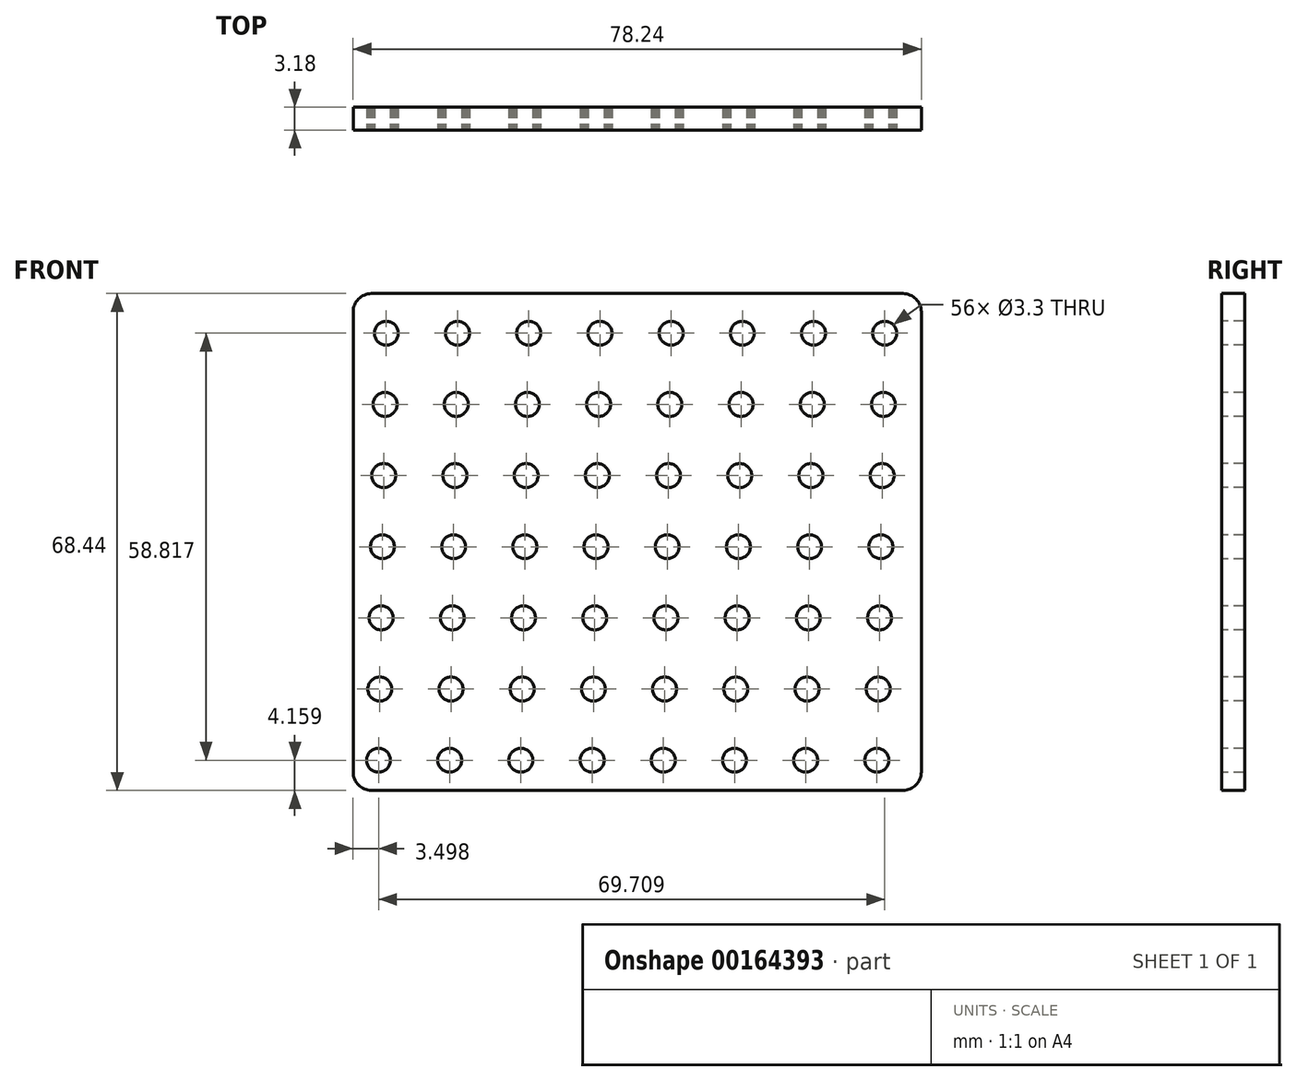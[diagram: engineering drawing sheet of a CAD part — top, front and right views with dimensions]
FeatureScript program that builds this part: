
annotation { "Feature Type Name" : "Feature", "Feature Type Description" : "" }
export const myFeature = defineFeature(function(context is Context, id is Id, definition is map)
    precondition{}
    {
        {
            var Q0;
            Q0=qCreatedBy(makeId("Front.planeOp"),FACE);
            var sketch = newSketch(context, id + "F0", { "sketchPlane" : qUnion([Q0])});
            skLineSegment(sketch, "E0.bottom", {"start": v(39.12, 34.22) * mm, "end": v(-39.12, 34.22) * mm});
            skLineSegment(sketch, "E0.top", {"start": v(39.12, -34.22) * mm, "end": v(-39.12, -34.22) * mm});
            skLineSegment(sketch, "E0.left", {"start": v(39.12, 34.22) * mm, "end": v(39.12, -34.22) * mm});
            skLineSegment(sketch, "E0.right", {"start": v(-39.12, 34.22) * mm, "end": v(-39.12, -34.22) * mm});
            skPoint(sketch, "E0.middle", {"position": v(0, 0) * mm});
            skSolve(sketch);
        }
        {
            var Q0;
            Q0=makeQuery(id+"F0.imprint","IMPRINT",FACE,{"disambiguationData":[TD([[makeQuery(id+"F0.imprint","IMPRINT",EDGE,{"derivedFrom":sQuery(id+"F0.wireOp",EDGE,"E0.bottom")}),1.0]])]});
            extrude(context, id + "F1", {"entities" : qUnion([Q0]), "depth" : 3.17 * mm});
        }
        {
            var Q0;
            Q0=makeQuery(id+"F1.opExtrude","CAP_FACE",FACE,{"disambiguationData":[OSD([sQuery(id+"F0.wireOp",EDGE,"E0.bottom"),sQuery(id+"F0.wireOp",EDGE,"E0.top"),sQuery(id+"F0.wireOp",EDGE,"E0.left"),sQuery(id+"F0.wireOp",EDGE,"E0.right")])],"isStart":false});
            var sketch = newSketch(context, id + "F2", { "sketchPlane" : qUnion([Q0])});
            skCircle(sketch, "E1", {"center": v(-34.54, 28.76) * mm, "radius": 1.65 * mm});
            skCircle(sketch, "E2.1.0.0", {"center": v(-24.74, 28.76) * mm, "radius": 1.65 * mm});
            skCircle(sketch, "E2.2.0.0", {"center": v(-14.94, 28.76) * mm, "radius": 1.65 * mm});
            skCircle(sketch, "E2.3.0.0", {"center": v(-5.13, 28.76) * mm, "radius": 1.65 * mm});
            skCircle(sketch, "E2.4.0.0", {"center": v(4.67, 28.76) * mm, "radius": 1.65 * mm});
            skCircle(sketch, "E2.5.0.0", {"center": v(14.48, 28.76) * mm, "radius": 1.65 * mm});
            skCircle(sketch, "E2.6.0.0", {"center": v(24.28, 28.76) * mm, "radius": 1.65 * mm});
            skCircle(sketch, "E2.7.0.0", {"center": v(34.09, 28.76) * mm, "radius": 1.65 * mm});
            skLineSegment(sketch, "E2.direction1", {"start": v(-34.54, 28.76) * mm, "end": v(-24.74, 28.76) * mm, "construction": true});
            skCircle(sketch, "E3.1.0.0", {"center": v(-34.72, 18.95) * mm, "radius": 1.65 * mm});
            skCircle(sketch, "E3.2.0.0", {"center": v(-34.9, 9.15) * mm, "radius": 1.65 * mm});
            skCircle(sketch, "E3.3.0.0", {"center": v(-35.08, -0.65) * mm, "radius": 1.65 * mm});
            skCircle(sketch, "E3.4.0.0", {"center": v(-35.26, -10.45) * mm, "radius": 1.65 * mm});
            skCircle(sketch, "E3.5.0.0", {"center": v(-35.44, -20.26) * mm, "radius": 1.65 * mm});
            skCircle(sketch, "E3.6.0.0", {"center": v(-35.62, -30.06) * mm, "radius": 1.65 * mm});
            skLineSegment(sketch, "E3.direction1", {"start": v(-34.54, 28.76) * mm, "end": v(-34.72, 18.95) * mm, "construction": true});
            skCircle(sketch, "E4.1.0.0", {"center": v(-24.92, 18.95) * mm, "radius": 1.65 * mm});
            skCircle(sketch, "E4.1.0.1", {"center": v(-25.1, 9.15) * mm, "radius": 1.65 * mm});
            skCircle(sketch, "E4.1.0.2", {"center": v(-25.28, -0.65) * mm, "radius": 1.65 * mm});
            skCircle(sketch, "E4.1.0.3", {"center": v(-25.46, -10.45) * mm, "radius": 1.65 * mm});
            skCircle(sketch, "E4.1.0.4", {"center": v(-25.64, -20.26) * mm, "radius": 1.65 * mm});
            skCircle(sketch, "E4.1.0.5", {"center": v(-25.82, -30.06) * mm, "radius": 1.65 * mm});
            skCircle(sketch, "E4.2.0.0", {"center": v(-15.11, 18.95) * mm, "radius": 1.65 * mm});
            skCircle(sketch, "E4.2.0.1", {"center": v(-15.3, 9.15) * mm, "radius": 1.65 * mm});
            skCircle(sketch, "E4.2.0.2", {"center": v(-15.47, -0.65) * mm, "radius": 1.65 * mm});
            skCircle(sketch, "E4.2.0.3", {"center": v(-15.65, -10.45) * mm, "radius": 1.65 * mm});
            skCircle(sketch, "E4.2.0.4", {"center": v(-15.83, -20.26) * mm, "radius": 1.65 * mm});
            skCircle(sketch, "E4.2.0.5", {"center": v(-16.01, -30.06) * mm, "radius": 1.65 * mm});
            skCircle(sketch, "E4.3.0.0", {"center": v(-5.31, 18.95) * mm, "radius": 1.65 * mm});
            skCircle(sketch, "E4.3.0.1", {"center": v(-5.5, 9.15) * mm, "radius": 1.65 * mm});
            skCircle(sketch, "E4.3.0.2", {"center": v(-5.67, -0.65) * mm, "radius": 1.65 * mm});
            skCircle(sketch, "E4.3.0.3", {"center": v(-5.85, -10.45) * mm, "radius": 1.65 * mm});
            skCircle(sketch, "E4.3.0.4", {"center": v(-6.03, -20.26) * mm, "radius": 1.65 * mm});
            skCircle(sketch, "E4.3.0.5", {"center": v(-6.2, -30.06) * mm, "radius": 1.65 * mm});
            skCircle(sketch, "E4.4.0.0", {"center": v(4.5, 18.95) * mm, "radius": 1.65 * mm});
            skCircle(sketch, "E4.4.0.1", {"center": v(4.31, 9.15) * mm, "radius": 1.65 * mm});
            skCircle(sketch, "E4.4.0.2", {"center": v(4.13, -0.65) * mm, "radius": 1.65 * mm});
            skCircle(sketch, "E4.4.0.3", {"center": v(3.95, -10.45) * mm, "radius": 1.65 * mm});
            skCircle(sketch, "E4.4.0.4", {"center": v(3.78, -20.26) * mm, "radius": 1.65 * mm});
            skCircle(sketch, "E4.4.0.5", {"center": v(3.6, -30.06) * mm, "radius": 1.65 * mm});
            skCircle(sketch, "E4.5.0.0", {"center": v(14.3, 18.95) * mm, "radius": 1.65 * mm});
            skCircle(sketch, "E4.5.0.1", {"center": v(14.12, 9.15) * mm, "radius": 1.65 * mm});
            skCircle(sketch, "E4.5.0.2", {"center": v(13.94, -0.65) * mm, "radius": 1.65 * mm});
            skCircle(sketch, "E4.5.0.3", {"center": v(13.76, -10.45) * mm, "radius": 1.65 * mm});
            skCircle(sketch, "E4.5.0.4", {"center": v(13.58, -20.26) * mm, "radius": 1.65 * mm});
            skCircle(sketch, "E4.5.0.5", {"center": v(13.4, -30.06) * mm, "radius": 1.65 * mm});
            skCircle(sketch, "E4.6.0.0", {"center": v(24.1, 18.95) * mm, "radius": 1.65 * mm});
            skCircle(sketch, "E4.6.0.1", {"center": v(23.92, 9.15) * mm, "radius": 1.65 * mm});
            skCircle(sketch, "E4.6.0.2", {"center": v(23.74, -0.65) * mm, "radius": 1.65 * mm});
            skCircle(sketch, "E4.6.0.3", {"center": v(23.56, -10.45) * mm, "radius": 1.65 * mm});
            skCircle(sketch, "E4.6.0.4", {"center": v(23.38, -20.26) * mm, "radius": 1.65 * mm});
            skCircle(sketch, "E4.6.0.5", {"center": v(23.2, -30.06) * mm, "radius": 1.65 * mm});
            skCircle(sketch, "E4.7.0.0", {"center": v(33.9, 18.95) * mm, "radius": 1.65 * mm});
            skCircle(sketch, "E4.7.0.1", {"center": v(33.73, 9.15) * mm, "radius": 1.65 * mm});
            skCircle(sketch, "E4.7.0.2", {"center": v(33.55, -0.65) * mm, "radius": 1.65 * mm});
            skCircle(sketch, "E4.7.0.3", {"center": v(33.37, -10.45) * mm, "radius": 1.65 * mm});
            skCircle(sketch, "E4.7.0.4", {"center": v(33.19, -20.26) * mm, "radius": 1.65 * mm});
            skCircle(sketch, "E4.7.0.5", {"center": v(33, -30.06) * mm, "radius": 1.65 * mm});
            skLineSegment(sketch, "E4.direction1", {"start": v(-34.72, 18.95) * mm, "end": v(-24.92, 18.95) * mm, "construction": true});
            skSolve(sketch);
        }
        {
            var Q0;
            Q0=sQuery(id+"F2.wireOp",VERTEX,"E4.4.0.4.center");
            var Q1;
            Q1=sQuery(id+"F2.wireOp",VERTEX,"E4.7.0.5.center");
            var Q2;
            Q2=sQuery(id+"F2.wireOp",VERTEX,"E4.1.0.0.center");
            var Q3;
            Q3=sQuery(id+"F2.wireOp",VERTEX,"E4.3.0.4.center");
            var Q4;
            Q4=sQuery(id+"F2.wireOp",VERTEX,"E4.7.0.2.center");
            var Q5;
            Q5=sQuery(id+"F2.wireOp",VERTEX,"E4.1.0.5.center");
            var Q6;
            Q6=sQuery(id+"F2.wireOp",VERTEX,"E4.2.0.3.center");
            var Q7;
            Q7=sQuery(id+"F2.wireOp",VERTEX,"E4.6.0.2.center");
            var Q8;
            Q8=sQuery(id+"F2.wireOp",VERTEX,"E4.3.0.3.center");
            var Q9;
            Q9=sQuery(id+"F2.wireOp",VERTEX,"E4.3.0.2.center");
            var Q10;
            Q10=sQuery(id+"F2.wireOp",VERTEX,"E2.5.0.0.center");
            var Q11;
            Q11=sQuery(id+"F2.wireOp",VERTEX,"E4.4.0.2.center");
            var Q12;
            Q12=sQuery(id+"F2.wireOp",VERTEX,"E3.6.0.0.center");
            var Q13;
            Q13=sQuery(id+"F2.wireOp",VERTEX,"E4.4.0.3.center");
            var Q14;
            Q14=sQuery(id+"F2.wireOp",VERTEX,"E4.7.0.1.center");
            var Q15;
            Q15=sQuery(id+"F2.wireOp",VERTEX,"E4.6.0.0.center");
            var Q16;
            Q16=sQuery(id+"F2.wireOp",VERTEX,"E3.2.0.0.center");
            var Q17;
            Q17=sQuery(id+"F2.wireOp",VERTEX,"E3.5.0.0.center");
            var Q18;
            Q18=sQuery(id+"F2.wireOp",VERTEX,"E4.1.0.4.center");
            var Q19;
            Q19=sQuery(id+"F2.wireOp",VERTEX,"E2.7.0.0.center");
            var Q20;
            Q20=sQuery(id+"F2.wireOp",VERTEX,"E2.6.0.0.center");
            var Q21;
            Q21=sQuery(id+"F2.wireOp",VERTEX,"E2.4.0.0.center");
            var Q22;
            Q22=sQuery(id+"F2.wireOp",VERTEX,"E2.3.0.0.center");
            var Q23;
            Q23=sQuery(id+"F2.wireOp",VERTEX,"E4.7.0.0.center");
            var Q24;
            Q24=sQuery(id+"F2.wireOp",VERTEX,"E4.3.0.1.center");
            var Q25;
            Q25=sQuery(id+"F2.wireOp",VERTEX,"E4.5.0.5.center");
            var Q26;
            Q26=sQuery(id+"F2.wireOp",VERTEX,"E2.2.0.0.center");
            var Q27;
            Q27=sQuery(id+"F2.wireOp",VERTEX,"E2.1.0.0.center");
            var Q28;
            Q28=sQuery(id+"F2.wireOp",VERTEX,"E3.4.0.0.center");
            var Q29;
            Q29=sQuery(id+"F2.wireOp",VERTEX,"E4.1.0.3.center");
            var Q30;
            Q30=sQuery(id+"F2.wireOp",VERTEX,"E4.4.0.1.center");
            var Q31;
            Q31=sQuery(id+"F2.wireOp",VERTEX,"E4.3.0.0.center");
            var Q32;
            Q32=sQuery(id+"F2.wireOp",VERTEX,"E4.6.0.5.center");
            var Q33;
            Q33=sQuery(id+"F2.wireOp",VERTEX,"E4.5.0.4.center");
            var Q34;
            Q34=sQuery(id+"F2.wireOp",VERTEX,"E3.3.0.0.center");
            var Q35;
            Q35=sQuery(id+"F2.wireOp",VERTEX,"E4.4.0.0.center");
            var Q36;
            Q36=sQuery(id+"F2.wireOp",VERTEX,"E4.2.0.5.center");
            var Q37;
            Q37=sQuery(id+"F2.wireOp",VERTEX,"E4.5.0.3.center");
            var Q38;
            Q38=sQuery(id+"F2.wireOp",VERTEX,"E4.6.0.4.center");
            var Q39;
            Q39=sQuery(id+"F2.wireOp",VERTEX,"E4.1.0.2.center");
            var Q40;
            Q40=sQuery(id+"F2.wireOp",VERTEX,"E4.2.0.2.center");
            var Q41;
            Q41=sQuery(id+"F2.wireOp",VERTEX,"E4.5.0.0.center");
            var Q42;
            Q42=sQuery(id+"F2.wireOp",VERTEX,"E4.7.0.4.center");
            var Q43;
            Q43=sQuery(id+"F2.wireOp",VERTEX,"E4.3.0.5.center");
            var Q44;
            Q44=sQuery(id+"F2.wireOp",VERTEX,"E4.2.0.4.center");
            var Q45;
            Q45=sQuery(id+"F2.wireOp",VERTEX,"E1.center");
            var Q46;
            Q46=sQuery(id+"F2.wireOp",VERTEX,"E4.5.0.2.center");
            var Q47;
            Q47=sQuery(id+"F2.wireOp",VERTEX,"E4.6.0.3.center");
            var Q48;
            Q48=sQuery(id+"F2.wireOp",VERTEX,"E4.1.0.1.center");
            var Q49;
            Q49=sQuery(id+"F2.wireOp",VERTEX,"E4.2.0.1.center");
            var Q50;
            Q50=sQuery(id+"F2.wireOp",VERTEX,"E4.4.0.5.center");
            var Q51;
            Q51=sQuery(id+"F2.wireOp",VERTEX,"E4.7.0.3.center");
            var Q52;
            Q52=sQuery(id+"F2.wireOp",VERTEX,"E4.direction1.start");
            var Q53;
            Q53=sQuery(id+"F2.wireOp",VERTEX,"E4.6.0.1.center");
            var Q54;
            Q54=sQuery(id+"F2.wireOp",VERTEX,"E4.2.0.0.center");
            var Q55;
            Q55=sQuery(id+"F2.wireOp",VERTEX,"E4.5.0.1.center");
            var Q56;
            Q56=makeQuery(id+"F1.opExtrude","SWEPT_BODY",BODY,{"disambiguationData":[OSD([sQuery(id+"F0.wireOp",EDGE,"E0.bottom"),sQuery(id+"F0.wireOp",EDGE,"E0.top"),sQuery(id+"F0.wireOp",EDGE,"E0.left"),sQuery(id+"F0.wireOp",EDGE,"E0.right")])]});
            hole(context, id + "F3", {"style" : HoleStyle.SIMPLE, "endStyle" : HoleEndStyle.THROUGH, "holeDiameter" : 3.3 * mm, "locations" : qUnion([Q0, Q1, Q2, Q3, Q4, Q5, Q6, Q7, Q8, Q9, Q10, Q11, Q12, Q13, Q14, Q15, Q16, Q17, Q18, Q19, Q20, Q21, Q22, Q23, Q24, Q25, Q26, Q27, Q28, Q29, Q30, Q31, Q32, Q33, Q34, Q35, Q36, Q37, Q38, Q39, Q40, Q41, Q42, Q43, Q44, Q45, Q46, Q47, Q48, Q49, Q50, Q51, Q52, Q53, Q54, Q55]), "scope" : qUnion([Q56]), "isTappedThrough" : true});
        }
        {
            var Q0;
            Q0=makeQuery(id+"F1.opExtrude","SWEPT_EDGE",EDGE,{"disambiguationData":[OSD([sQuery(id+"F0.wireOp",EDGE,"E0.bottom"),sQuery(id+"F0.wireOp",EDGE,"E0.right")])]});
            var Q1;
            Q1=makeQuery(id+"F1.opExtrude","SWEPT_EDGE",EDGE,{"disambiguationData":[OSD([sQuery(id+"F0.wireOp",EDGE,"E0.top"),sQuery(id+"F0.wireOp",EDGE,"E0.right")])]});
            var Q2;
            Q2=makeQuery(id+"F1.opExtrude","SWEPT_EDGE",EDGE,{"disambiguationData":[OSD([sQuery(id+"F0.wireOp",EDGE,"E0.top"),sQuery(id+"F0.wireOp",EDGE,"E0.left")])]});
            var Q3;
            Q3=makeQuery(id+"F1.opExtrude","SWEPT_EDGE",EDGE,{"disambiguationData":[OSD([sQuery(id+"F0.wireOp",EDGE,"E0.bottom"),sQuery(id+"F0.wireOp",EDGE,"E0.left")])]});
            fillet(context, id + "F4", {"entities" : qUnion([Q0, Q1, Q2, Q3]), "radius" : 2.54 * mm, "tangentPropagation" : true, "allowEdgeOverflow" : false});
        }
    });
